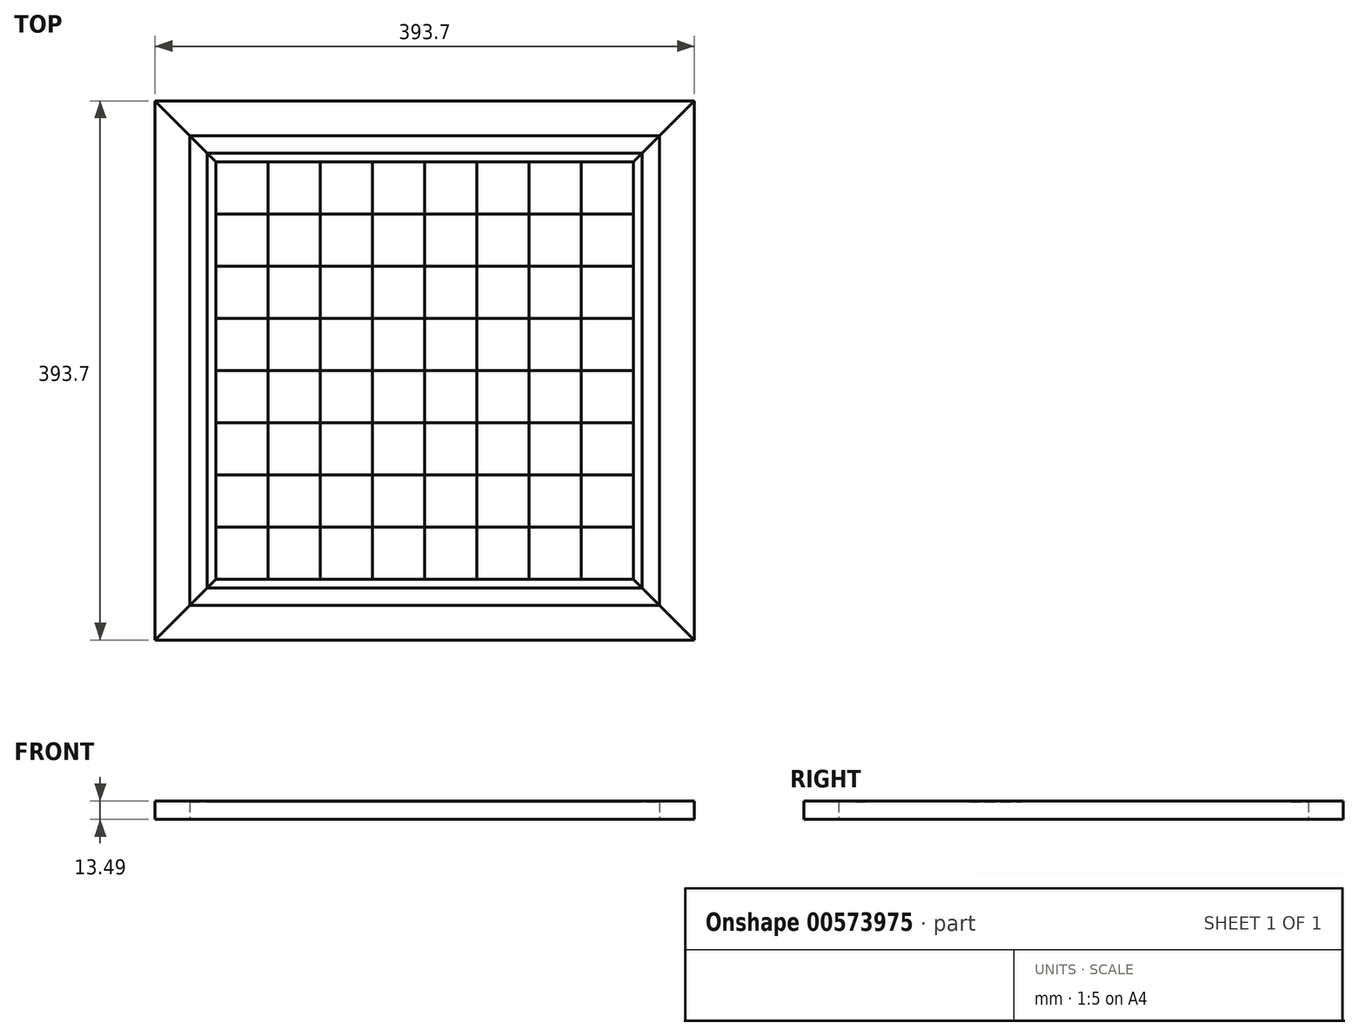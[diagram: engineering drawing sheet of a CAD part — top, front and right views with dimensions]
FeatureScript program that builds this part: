
annotation { "Feature Type Name" : "Feature", "Feature Type Description" : "" }
export const myFeature = defineFeature(function(context is Context, id is Id, definition is map)
    precondition{}
    {
        {
            var Q0;
            Q0=qCreatedBy(makeId("Top.planeOp"),FACE);
            var sketch = newSketch(context, id + "F0", { "sketchPlane" : qUnion([Q0])});
            skLineSegment(sketch, "E0.bottom", {"start": v(-171.45, 171.45) * mm, "end": v(171.45, 171.45) * mm});
            skLineSegment(sketch, "E0.top", {"start": v(-171.45, -171.45) * mm, "end": v(171.45, -171.45) * mm});
            skLineSegment(sketch, "E0.left", {"start": v(-171.45, 171.45) * mm, "end": v(-171.45, -171.45) * mm});
            skLineSegment(sketch, "E0.right", {"start": v(171.45, 171.45) * mm, "end": v(171.45, -171.45) * mm});
            skPoint(sketch, "E0.middle", {"position": v(0, 0) * mm});
            skSolve(sketch);
        }
        {
            var Q0;
            Q0 = qSketchRegion(id + "F0", true);
            extrude(context, id + "F1", {"entities" : qUnion([Q0]), "depth" : 12.7 * mm, "offsetDistance" : 25.4 * mm});
        }
        {
            var Q0;
            Q0=makeQuery(id+"F1.opExtrude","CAP_FACE",FACE,{"disambiguationData":[OSD([sQuery(id+"F0.wireOp",EDGE,"E0.bottom"),sQuery(id+"F0.wireOp",EDGE,"E0.top"),sQuery(id+"F0.wireOp",EDGE,"E0.left"),sQuery(id+"F0.wireOp",EDGE,"E0.right")])],"isStart":false});
            var sketch = newSketch(context, id + "F2", { "sketchPlane" : qUnion([Q0])});
            skLineSegment(sketch, "E1", {"start": v(152.4, 152.4) * mm, "end": v(152.4, -152.4) * mm});
            skLineSegment(sketch, "E2", {"start": v(171.45, -171.45) * mm, "end": v(152.4, -152.4) * mm});
            skLineSegment(sketch, "E3", {"start": v(171.45, 171.45) * mm, "end": v(152.4, 152.4) * mm});
            skLineSegment(sketch, "E4", {"start": v(152.4, 152.4) * mm, "end": v(-152.4, 152.4) * mm});
            skLineSegment(sketch, "E5", {"start": v(-152.4, 152.4) * mm, "end": v(-152.4, -152.4) * mm});
            skLineSegment(sketch, "E6", {"start": v(-152.4, -152.4) * mm, "end": v(152.4, -152.4) * mm});
            skLineSegment(sketch, "E7.trimOffspring", {"start": v(-152.4, -152.4) * mm, "end": v(-171.45, -171.45) * mm});
            skLineSegment(sketch, "E8.trimOffspring", {"start": v(-152.4, 152.4) * mm, "end": v(-171.45, 171.45) * mm});
            skLineSegment(sketch, "E9", {"start": v(158.75, 158.75) * mm, "end": v(158.75, -158.75) * mm});
            skLineSegment(sketch, "E10", {"start": v(158.75, 158.75) * mm, "end": v(-158.75, 158.75) * mm});
            skLineSegment(sketch, "E11", {"start": v(-158.75, 158.75) * mm, "end": v(-158.75, -158.75) * mm});
            skLineSegment(sketch, "E12", {"start": v(-158.75, -158.75) * mm, "end": v(158.75, -158.75) * mm});
            skLineSegment(sketch, "E13", {"start": v(152.4, 114.3) * mm, "end": v(-152.4, 114.3) * mm});
            skLineSegment(sketch, "E14", {"start": v(152.4, 76.2) * mm, "end": v(-152.4, 76.2) * mm});
            skLineSegment(sketch, "E15", {"start": v(152.4, 38.1) * mm, "end": v(-152.4, 38.1) * mm});
            skLineSegment(sketch, "E16", {"start": v(152.4, 0) * mm, "end": v(-152.4, 0) * mm});
            skLineSegment(sketch, "E17", {"start": v(152.4, -38.1) * mm, "end": v(-152.4, -38.1) * mm});
            skLineSegment(sketch, "E18", {"start": v(152.4, -76.2) * mm, "end": v(-152.4, -76.2) * mm});
            skLineSegment(sketch, "E19", {"start": v(-152.4, -114.3) * mm, "end": v(152.4, -114.3) * mm});
            skLineSegment(sketch, "E20", {"start": v(114.3, 152.4) * mm, "end": v(114.3, -152.4) * mm});
            skLineSegment(sketch, "E21", {"start": v(76.2, 152.4) * mm, "end": v(76.2, -152.4) * mm});
            skLineSegment(sketch, "E22", {"start": v(38.1, 152.4) * mm, "end": v(38.1, -152.4) * mm});
            skLineSegment(sketch, "E23", {"start": v(-114.3, 152.4) * mm, "end": v(-114.3, -152.4) * mm});
            skLineSegment(sketch, "E24", {"start": v(0, 152.4) * mm, "end": v(0, -152.4) * mm});
            skLineSegment(sketch, "E25", {"start": v(-38.1, 152.4) * mm, "end": v(-38.1, -152.4) * mm});
            skLineSegment(sketch, "E26", {"start": v(-76.2, -152.4) * mm, "end": v(-76.2, 152.4) * mm});
            skSolve(sketch);
        }
        {
            var Q0;
            {var subQ1=sQuery(id+"F2.wireOp",EDGE,"E1");var subQ3=sQuery(id+"F2.wireOp",EDGE,"E13");var subQ4=makeQuery(id+"F2.imprint","INTERSECT",VERTEX,{"derivedFrom":[subQ1,subQ3]});Q0=makeQuery(id+"F2.imprint","IMPRINT",FACE,{"disambiguationData":[TD([[makeQuery(id+"F2.imprint","IMPRINT",EDGE,{"disambiguationData":[TD([[subQ4,-1.0]])],"derivedFrom":subQ3}),-1.0]])]});}
            var Q1;
            {var subQ0=sQuery(id+"F2.wireOp",EDGE,"E14");var subQ1=sQuery(id+"F2.wireOp",EDGE,"E1");var subQ2=makeQuery(id+"F2.imprint","INTERSECT",VERTEX,{"derivedFrom":[subQ1,subQ0]});Q1=makeQuery(id+"F2.imprint","IMPRINT",FACE,{"disambiguationData":[TD([[makeQuery(id+"F2.imprint","IMPRINT",EDGE,{"disambiguationData":[TD([[subQ2,-1.0]])],"derivedFrom":subQ1}),-1.0]])]});}
            var Q2;
            {var subQ0=sQuery(id+"F2.wireOp",EDGE,"E16");var subQ1=sQuery(id+"F2.wireOp",EDGE,"E1");var subQ2=makeQuery(id+"F2.imprint","INTERSECT",VERTEX,{"derivedFrom":[subQ1,subQ0]});Q2=makeQuery(id+"F2.imprint","IMPRINT",FACE,{"disambiguationData":[TD([[makeQuery(id+"F2.imprint","IMPRINT",EDGE,{"disambiguationData":[TD([[subQ2,-1.0]])],"derivedFrom":subQ1}),-1.0]])]});}
            var Q3;
            {var subQ0=sQuery(id+"F2.wireOp",EDGE,"E18");var subQ1=sQuery(id+"F2.wireOp",EDGE,"E1");var subQ2=makeQuery(id+"F2.imprint","INTERSECT",VERTEX,{"derivedFrom":[subQ1,subQ0]});Q3=makeQuery(id+"F2.imprint","IMPRINT",FACE,{"disambiguationData":[TD([[makeQuery(id+"F2.imprint","IMPRINT",EDGE,{"disambiguationData":[TD([[subQ2,-1.0]])],"derivedFrom":subQ1}),-1.0]])]});}
            var Q4;
            {var subQ0=sQuery(id+"F2.wireOp",EDGE,"E20");var subQ1=sQuery(id+"F2.wireOp",EDGE,"E6");var subQ2=makeQuery(id+"F2.imprint","INTERSECT",VERTEX,{"derivedFrom":[subQ1,subQ0]});Q4=makeQuery(id+"F2.imprint","IMPRINT",FACE,{"disambiguationData":[TD([[makeQuery(id+"F2.imprint","IMPRINT",EDGE,{"disambiguationData":[TD([[subQ2,1.0]])],"derivedFrom":subQ1}),1.0]])]});}
            var Q5;
            {var subQ0=sQuery(id+"F2.wireOp",EDGE,"E20");var subQ1=sQuery(id+"F2.wireOp",EDGE,"E17");var subQ2=makeQuery(id+"F2.imprint","INTERSECT",VERTEX,{"derivedFrom":[subQ1,subQ0]});Q5=makeQuery(id+"F2.imprint","IMPRINT",FACE,{"disambiguationData":[TD([[makeQuery(id+"F2.imprint","IMPRINT",EDGE,{"disambiguationData":[TD([[subQ2,-1.0]])],"derivedFrom":subQ1}),1.0]])]});}
            var Q6;
            {var subQ0=sQuery(id+"F2.wireOp",EDGE,"E20");var subQ1=sQuery(id+"F2.wireOp",EDGE,"E15");var subQ2=makeQuery(id+"F2.imprint","INTERSECT",VERTEX,{"derivedFrom":[subQ1,subQ0]});Q6=makeQuery(id+"F2.imprint","IMPRINT",FACE,{"disambiguationData":[TD([[makeQuery(id+"F2.imprint","IMPRINT",EDGE,{"disambiguationData":[TD([[subQ2,-1.0]])],"derivedFrom":subQ1}),1.0]])]});}
            var Q7;
            {var subQ0=sQuery(id+"F2.wireOp",EDGE,"E20");var subQ1=sQuery(id+"F2.wireOp",EDGE,"E13");var subQ2=makeQuery(id+"F2.imprint","INTERSECT",VERTEX,{"derivedFrom":[subQ1,subQ0]});Q7=makeQuery(id+"F2.imprint","IMPRINT",FACE,{"disambiguationData":[TD([[makeQuery(id+"F2.imprint","IMPRINT",EDGE,{"disambiguationData":[TD([[subQ2,-1.0]])],"derivedFrom":subQ1}),1.0]])]});}
            var Q8;
            {var subQ0=sQuery(id+"F2.wireOp",EDGE,"E21");var subQ1=sQuery(id+"F2.wireOp",EDGE,"E4");var subQ2=makeQuery(id+"F2.imprint","INTERSECT",VERTEX,{"derivedFrom":[subQ1,subQ0]});Q8=makeQuery(id+"F2.imprint","IMPRINT",FACE,{"disambiguationData":[TD([[makeQuery(id+"F2.imprint","IMPRINT",EDGE,{"disambiguationData":[TD([[subQ2,-1.0]])],"derivedFrom":subQ1}),1.0]])]});}
            var Q9;
            {var subQ0=sQuery(id+"F2.wireOp",EDGE,"E21");var subQ1=sQuery(id+"F2.wireOp",EDGE,"E14");var subQ2=makeQuery(id+"F2.imprint","INTERSECT",VERTEX,{"derivedFrom":[subQ1,subQ0]});Q9=makeQuery(id+"F2.imprint","IMPRINT",FACE,{"disambiguationData":[TD([[makeQuery(id+"F2.imprint","IMPRINT",EDGE,{"disambiguationData":[TD([[subQ2,-1.0]])],"derivedFrom":subQ1}),1.0]])]});}
            var Q10;
            {var subQ0=sQuery(id+"F2.wireOp",EDGE,"E21");var subQ1=sQuery(id+"F2.wireOp",EDGE,"E16");var subQ2=makeQuery(id+"F2.imprint","INTERSECT",VERTEX,{"derivedFrom":[subQ1,subQ0]});Q10=makeQuery(id+"F2.imprint","IMPRINT",FACE,{"disambiguationData":[TD([[makeQuery(id+"F2.imprint","IMPRINT",EDGE,{"disambiguationData":[TD([[subQ2,-1.0]])],"derivedFrom":subQ1}),1.0]])]});}
            var Q11;
            {var subQ0=sQuery(id+"F2.wireOp",EDGE,"E21");var subQ1=sQuery(id+"F2.wireOp",EDGE,"E18");var subQ2=makeQuery(id+"F2.imprint","INTERSECT",VERTEX,{"derivedFrom":[subQ1,subQ0]});Q11=makeQuery(id+"F2.imprint","IMPRINT",FACE,{"disambiguationData":[TD([[makeQuery(id+"F2.imprint","IMPRINT",EDGE,{"disambiguationData":[TD([[subQ2,-1.0]])],"derivedFrom":subQ1}),1.0]])]});}
            var Q12;
            {var subQ0=sQuery(id+"F2.wireOp",EDGE,"E22");var subQ1=sQuery(id+"F2.wireOp",EDGE,"E13");var subQ2=makeQuery(id+"F2.imprint","INTERSECT",VERTEX,{"derivedFrom":[subQ1,subQ0]});Q12=makeQuery(id+"F2.imprint","IMPRINT",FACE,{"disambiguationData":[TD([[makeQuery(id+"F2.imprint","IMPRINT",EDGE,{"disambiguationData":[TD([[subQ2,-1.0]])],"derivedFrom":subQ1}),1.0]])]});}
            var Q13;
            {var subQ0=sQuery(id+"F2.wireOp",EDGE,"E22");var subQ1=sQuery(id+"F2.wireOp",EDGE,"E15");var subQ2=makeQuery(id+"F2.imprint","INTERSECT",VERTEX,{"derivedFrom":[subQ1,subQ0]});Q13=makeQuery(id+"F2.imprint","IMPRINT",FACE,{"disambiguationData":[TD([[makeQuery(id+"F2.imprint","IMPRINT",EDGE,{"disambiguationData":[TD([[subQ2,-1.0]])],"derivedFrom":subQ1}),1.0]])]});}
            var Q14;
            {var subQ0=sQuery(id+"F2.wireOp",EDGE,"E22");var subQ1=sQuery(id+"F2.wireOp",EDGE,"E17");var subQ2=makeQuery(id+"F2.imprint","INTERSECT",VERTEX,{"derivedFrom":[subQ1,subQ0]});Q14=makeQuery(id+"F2.imprint","IMPRINT",FACE,{"disambiguationData":[TD([[makeQuery(id+"F2.imprint","IMPRINT",EDGE,{"disambiguationData":[TD([[subQ2,-1.0]])],"derivedFrom":subQ1}),1.0]])]});}
            var Q15;
            {var subQ0=sQuery(id+"F2.wireOp",EDGE,"E22");var subQ1=sQuery(id+"F2.wireOp",EDGE,"E6");var subQ2=makeQuery(id+"F2.imprint","INTERSECT",VERTEX,{"derivedFrom":[subQ1,subQ0]});Q15=makeQuery(id+"F2.imprint","IMPRINT",FACE,{"disambiguationData":[TD([[makeQuery(id+"F2.imprint","IMPRINT",EDGE,{"disambiguationData":[TD([[subQ2,1.0]])],"derivedFrom":subQ1}),1.0]])]});}
            var Q16;
            {var subQ0=sQuery(id+"F2.wireOp",EDGE,"E24");var subQ1=sQuery(id+"F2.wireOp",EDGE,"E18");var subQ2=makeQuery(id+"F2.imprint","INTERSECT",VERTEX,{"derivedFrom":[subQ1,subQ0]});Q16=makeQuery(id+"F2.imprint","IMPRINT",FACE,{"disambiguationData":[TD([[makeQuery(id+"F2.imprint","IMPRINT",EDGE,{"disambiguationData":[TD([[subQ2,-1.0]])],"derivedFrom":subQ1}),1.0]])]});}
            var Q17;
            {var subQ0=sQuery(id+"F2.wireOp",EDGE,"E24");var subQ1=sQuery(id+"F2.wireOp",EDGE,"E16");var subQ2=makeQuery(id+"F2.imprint","INTERSECT",VERTEX,{"derivedFrom":[subQ1,subQ0]});Q17=makeQuery(id+"F2.imprint","IMPRINT",FACE,{"disambiguationData":[TD([[makeQuery(id+"F2.imprint","IMPRINT",EDGE,{"disambiguationData":[TD([[subQ2,-1.0]])],"derivedFrom":subQ1}),1.0]])]});}
            var Q18;
            {var subQ0=sQuery(id+"F2.wireOp",EDGE,"E24");var subQ1=sQuery(id+"F2.wireOp",EDGE,"E14");var subQ2=makeQuery(id+"F2.imprint","INTERSECT",VERTEX,{"derivedFrom":[subQ1,subQ0]});Q18=makeQuery(id+"F2.imprint","IMPRINT",FACE,{"disambiguationData":[TD([[makeQuery(id+"F2.imprint","IMPRINT",EDGE,{"disambiguationData":[TD([[subQ2,-1.0]])],"derivedFrom":subQ1}),1.0]])]});}
            var Q19;
            {var subQ0=sQuery(id+"F2.wireOp",EDGE,"E24");var subQ1=sQuery(id+"F2.wireOp",EDGE,"E4");var subQ2=makeQuery(id+"F2.imprint","INTERSECT",VERTEX,{"derivedFrom":[subQ1,subQ0]});Q19=makeQuery(id+"F2.imprint","IMPRINT",FACE,{"disambiguationData":[TD([[makeQuery(id+"F2.imprint","IMPRINT",EDGE,{"disambiguationData":[TD([[subQ2,-1.0]])],"derivedFrom":subQ1}),1.0]])]});}
            var Q20;
            {var subQ0=sQuery(id+"F2.wireOp",EDGE,"E25");var subQ1=sQuery(id+"F2.wireOp",EDGE,"E13");var subQ2=makeQuery(id+"F2.imprint","INTERSECT",VERTEX,{"derivedFrom":[subQ1,subQ0]});Q20=makeQuery(id+"F2.imprint","IMPRINT",FACE,{"disambiguationData":[TD([[makeQuery(id+"F2.imprint","IMPRINT",EDGE,{"disambiguationData":[TD([[subQ2,-1.0]])],"derivedFrom":subQ1}),1.0]])]});}
            var Q21;
            {var subQ0=sQuery(id+"F2.wireOp",EDGE,"E25");var subQ1=sQuery(id+"F2.wireOp",EDGE,"E15");var subQ2=makeQuery(id+"F2.imprint","INTERSECT",VERTEX,{"derivedFrom":[subQ1,subQ0]});Q21=makeQuery(id+"F2.imprint","IMPRINT",FACE,{"disambiguationData":[TD([[makeQuery(id+"F2.imprint","IMPRINT",EDGE,{"disambiguationData":[TD([[subQ2,-1.0]])],"derivedFrom":subQ1}),1.0]])]});}
            var Q22;
            {var subQ0=sQuery(id+"F2.wireOp",EDGE,"E25");var subQ1=sQuery(id+"F2.wireOp",EDGE,"E17");var subQ2=makeQuery(id+"F2.imprint","INTERSECT",VERTEX,{"derivedFrom":[subQ1,subQ0]});Q22=makeQuery(id+"F2.imprint","IMPRINT",FACE,{"disambiguationData":[TD([[makeQuery(id+"F2.imprint","IMPRINT",EDGE,{"disambiguationData":[TD([[subQ2,-1.0]])],"derivedFrom":subQ1}),1.0]])]});}
            var Q23;
            {var subQ0=sQuery(id+"F2.wireOp",EDGE,"E25");var subQ1=sQuery(id+"F2.wireOp",EDGE,"E6");var subQ2=makeQuery(id+"F2.imprint","INTERSECT",VERTEX,{"derivedFrom":[subQ1,subQ0]});Q23=makeQuery(id+"F2.imprint","IMPRINT",FACE,{"disambiguationData":[TD([[makeQuery(id+"F2.imprint","IMPRINT",EDGE,{"disambiguationData":[TD([[subQ2,1.0]])],"derivedFrom":subQ1}),1.0]])]});}
            var Q24;
            {var subQ0=sQuery(id+"F2.wireOp",EDGE,"E26");var subQ1=sQuery(id+"F2.wireOp",EDGE,"E18");var subQ2=makeQuery(id+"F2.imprint","INTERSECT",VERTEX,{"derivedFrom":[subQ1,subQ0]});Q24=makeQuery(id+"F2.imprint","IMPRINT",FACE,{"disambiguationData":[TD([[makeQuery(id+"F2.imprint","IMPRINT",EDGE,{"disambiguationData":[TD([[subQ2,-1.0]])],"derivedFrom":subQ1}),1.0]])]});}
            var Q25;
            {var subQ0=sQuery(id+"F2.wireOp",EDGE,"E26");var subQ1=sQuery(id+"F2.wireOp",EDGE,"E16");var subQ2=makeQuery(id+"F2.imprint","INTERSECT",VERTEX,{"derivedFrom":[subQ1,subQ0]});Q25=makeQuery(id+"F2.imprint","IMPRINT",FACE,{"disambiguationData":[TD([[makeQuery(id+"F2.imprint","IMPRINT",EDGE,{"disambiguationData":[TD([[subQ2,-1.0]])],"derivedFrom":subQ1}),1.0]])]});}
            var Q26;
            {var subQ0=sQuery(id+"F2.wireOp",EDGE,"E26");var subQ1=sQuery(id+"F2.wireOp",EDGE,"E14");var subQ2=makeQuery(id+"F2.imprint","INTERSECT",VERTEX,{"derivedFrom":[subQ1,subQ0]});Q26=makeQuery(id+"F2.imprint","IMPRINT",FACE,{"disambiguationData":[TD([[makeQuery(id+"F2.imprint","IMPRINT",EDGE,{"disambiguationData":[TD([[subQ2,-1.0]])],"derivedFrom":subQ1}),1.0]])]});}
            var Q27;
            {var subQ0=sQuery(id+"F2.wireOp",EDGE,"E23");var subQ1=sQuery(id+"F2.wireOp",EDGE,"E4");var subQ2=makeQuery(id+"F2.imprint","INTERSECT",VERTEX,{"derivedFrom":[subQ1,subQ0]});Q27=makeQuery(id+"F2.imprint","IMPRINT",FACE,{"disambiguationData":[TD([[makeQuery(id+"F2.imprint","IMPRINT",EDGE,{"disambiguationData":[TD([[subQ2,1.0]])],"derivedFrom":subQ1}),1.0]])]});}
            var Q28;
            {var subQ0=sQuery(id+"F2.wireOp",EDGE,"E13");var subQ1=sQuery(id+"F2.wireOp",EDGE,"E5");var subQ2=makeQuery(id+"F2.imprint","INTERSECT",VERTEX,{"derivedFrom":[subQ1,subQ0]});Q28=makeQuery(id+"F2.imprint","IMPRINT",FACE,{"disambiguationData":[TD([[makeQuery(id+"F2.imprint","IMPRINT",EDGE,{"disambiguationData":[TD([[subQ2,-1.0]])],"derivedFrom":subQ1}),1.0]])]});}
            var Q29;
            {var subQ0=sQuery(id+"F2.wireOp",EDGE,"E15");var subQ1=sQuery(id+"F2.wireOp",EDGE,"E5");var subQ2=makeQuery(id+"F2.imprint","INTERSECT",VERTEX,{"derivedFrom":[subQ1,subQ0]});Q29=makeQuery(id+"F2.imprint","IMPRINT",FACE,{"disambiguationData":[TD([[makeQuery(id+"F2.imprint","IMPRINT",EDGE,{"disambiguationData":[TD([[subQ2,-1.0]])],"derivedFrom":subQ1}),1.0]])]});}
            var Q30;
            {var subQ0=sQuery(id+"F2.wireOp",EDGE,"E17");var subQ1=sQuery(id+"F2.wireOp",EDGE,"E5");var subQ2=makeQuery(id+"F2.imprint","INTERSECT",VERTEX,{"derivedFrom":[subQ1,subQ0]});Q30=makeQuery(id+"F2.imprint","IMPRINT",FACE,{"disambiguationData":[TD([[makeQuery(id+"F2.imprint","IMPRINT",EDGE,{"disambiguationData":[TD([[subQ2,-1.0]])],"derivedFrom":subQ1}),1.0]])]});}
            var Q31;
            {var subQ1=sQuery(id+"F2.wireOp",EDGE,"E5");var subQ3=sQuery(id+"F2.wireOp",EDGE,"E19");var subQ4=makeQuery(id+"F2.imprint","INTERSECT",VERTEX,{"derivedFrom":[subQ1,subQ3]});Q31=makeQuery(id+"F2.imprint","IMPRINT",FACE,{"disambiguationData":[TD([[makeQuery(id+"F2.imprint","IMPRINT",EDGE,{"disambiguationData":[TD([[subQ4,-1.0]])],"derivedFrom":subQ3}),-1.0]])]});}
            extrude(context, id + "F3", {"entities" : qUnion([Q0, Q1, Q2, Q3, Q4, Q5, Q6, Q7, Q8, Q9, Q10, Q11, Q12, Q13, Q14, Q15, Q16, Q17, Q18, Q19, Q20, Q21, Q22, Q23, Q24, Q25, Q26, Q27, Q28, Q29, Q30, Q31]), "depth" : 0.8 * mm, "offsetDistance" : 25.4 * mm});
        }
        {
            var Q0;
            {var subQ0=sQuery(id+"F2.wireOp",EDGE,"E13");var subQ1=sQuery(id+"F2.wireOp",EDGE,"E1");var subQ2=makeQuery(id+"F2.imprint","INTERSECT",VERTEX,{"derivedFrom":[subQ1,subQ0]});Q0=makeQuery(id+"F2.imprint","IMPRINT",FACE,{"disambiguationData":[TD([[makeQuery(id+"F2.imprint","IMPRINT",EDGE,{"disambiguationData":[TD([[subQ2,-1.0]])],"derivedFrom":subQ1}),-1.0]])]});}
            var Q1;
            {var subQ0=sQuery(id+"F2.wireOp",EDGE,"E15");var subQ1=sQuery(id+"F2.wireOp",EDGE,"E1");var subQ2=makeQuery(id+"F2.imprint","INTERSECT",VERTEX,{"derivedFrom":[subQ1,subQ0]});Q1=makeQuery(id+"F2.imprint","IMPRINT",FACE,{"disambiguationData":[TD([[makeQuery(id+"F2.imprint","IMPRINT",EDGE,{"disambiguationData":[TD([[subQ2,-1.0]])],"derivedFrom":subQ1}),-1.0]])]});}
            var Q2;
            {var subQ0=sQuery(id+"F2.wireOp",EDGE,"E17");var subQ1=sQuery(id+"F2.wireOp",EDGE,"E1");var subQ2=makeQuery(id+"F2.imprint","INTERSECT",VERTEX,{"derivedFrom":[subQ1,subQ0]});Q2=makeQuery(id+"F2.imprint","IMPRINT",FACE,{"disambiguationData":[TD([[makeQuery(id+"F2.imprint","IMPRINT",EDGE,{"disambiguationData":[TD([[subQ2,-1.0]])],"derivedFrom":subQ1}),-1.0]])]});}
            var Q3;
            {var subQ1=sQuery(id+"F2.wireOp",EDGE,"E1");var subQ3=sQuery(id+"F2.wireOp",EDGE,"E19");var subQ4=makeQuery(id+"F2.imprint","INTERSECT",VERTEX,{"derivedFrom":[subQ1,subQ3]});Q3=makeQuery(id+"F2.imprint","IMPRINT",FACE,{"disambiguationData":[TD([[makeQuery(id+"F2.imprint","IMPRINT",EDGE,{"disambiguationData":[TD([[subQ4,1.0]])],"derivedFrom":subQ3}),-1.0]])]});}
            var Q4;
            {var subQ0=sQuery(id+"F2.wireOp",EDGE,"E20");var subQ1=sQuery(id+"F2.wireOp",EDGE,"E16");var subQ2=makeQuery(id+"F2.imprint","INTERSECT",VERTEX,{"derivedFrom":[subQ1,subQ0]});Q4=makeQuery(id+"F2.imprint","IMPRINT",FACE,{"disambiguationData":[TD([[makeQuery(id+"F2.imprint","IMPRINT",EDGE,{"disambiguationData":[TD([[subQ2,-1.0]])],"derivedFrom":subQ1}),1.0]])]});}
            var Q5;
            {var subQ0=sQuery(id+"F2.wireOp",EDGE,"E20");var subQ1=sQuery(id+"F2.wireOp",EDGE,"E14");var subQ2=makeQuery(id+"F2.imprint","INTERSECT",VERTEX,{"derivedFrom":[subQ1,subQ0]});Q5=makeQuery(id+"F2.imprint","IMPRINT",FACE,{"disambiguationData":[TD([[makeQuery(id+"F2.imprint","IMPRINT",EDGE,{"disambiguationData":[TD([[subQ2,-1.0]])],"derivedFrom":subQ1}),1.0]])]});}
            var Q6;
            {var subQ0=sQuery(id+"F2.wireOp",EDGE,"E20");var subQ1=sQuery(id+"F2.wireOp",EDGE,"E4");var subQ2=makeQuery(id+"F2.imprint","INTERSECT",VERTEX,{"derivedFrom":[subQ1,subQ0]});Q6=makeQuery(id+"F2.imprint","IMPRINT",FACE,{"disambiguationData":[TD([[makeQuery(id+"F2.imprint","IMPRINT",EDGE,{"disambiguationData":[TD([[subQ2,-1.0]])],"derivedFrom":subQ1}),1.0]])]});}
            var Q7;
            {var subQ0=sQuery(id+"F2.wireOp",EDGE,"E21");var subQ1=sQuery(id+"F2.wireOp",EDGE,"E13");var subQ2=makeQuery(id+"F2.imprint","INTERSECT",VERTEX,{"derivedFrom":[subQ1,subQ0]});Q7=makeQuery(id+"F2.imprint","IMPRINT",FACE,{"disambiguationData":[TD([[makeQuery(id+"F2.imprint","IMPRINT",EDGE,{"disambiguationData":[TD([[subQ2,-1.0]])],"derivedFrom":subQ1}),1.0]])]});}
            var Q8;
            {var subQ0=sQuery(id+"F2.wireOp",EDGE,"E21");var subQ1=sQuery(id+"F2.wireOp",EDGE,"E15");var subQ2=makeQuery(id+"F2.imprint","INTERSECT",VERTEX,{"derivedFrom":[subQ1,subQ0]});Q8=makeQuery(id+"F2.imprint","IMPRINT",FACE,{"disambiguationData":[TD([[makeQuery(id+"F2.imprint","IMPRINT",EDGE,{"disambiguationData":[TD([[subQ2,-1.0]])],"derivedFrom":subQ1}),1.0]])]});}
            var Q9;
            {var subQ0=sQuery(id+"F2.wireOp",EDGE,"E21");var subQ1=sQuery(id+"F2.wireOp",EDGE,"E17");var subQ2=makeQuery(id+"F2.imprint","INTERSECT",VERTEX,{"derivedFrom":[subQ1,subQ0]});Q9=makeQuery(id+"F2.imprint","IMPRINT",FACE,{"disambiguationData":[TD([[makeQuery(id+"F2.imprint","IMPRINT",EDGE,{"disambiguationData":[TD([[subQ2,-1.0]])],"derivedFrom":subQ1}),1.0]])]});}
            var Q10;
            {var subQ0=sQuery(id+"F2.wireOp",EDGE,"E21");var subQ1=sQuery(id+"F2.wireOp",EDGE,"E6");var subQ2=makeQuery(id+"F2.imprint","INTERSECT",VERTEX,{"derivedFrom":[subQ1,subQ0]});Q10=makeQuery(id+"F2.imprint","IMPRINT",FACE,{"disambiguationData":[TD([[makeQuery(id+"F2.imprint","IMPRINT",EDGE,{"disambiguationData":[TD([[subQ2,1.0]])],"derivedFrom":subQ1}),1.0]])]});}
            var Q11;
            {var subQ0=sQuery(id+"F2.wireOp",EDGE,"E20");var subQ1=sQuery(id+"F2.wireOp",EDGE,"E18");var subQ2=makeQuery(id+"F2.imprint","INTERSECT",VERTEX,{"derivedFrom":[subQ1,subQ0]});Q11=makeQuery(id+"F2.imprint","IMPRINT",FACE,{"disambiguationData":[TD([[makeQuery(id+"F2.imprint","IMPRINT",EDGE,{"disambiguationData":[TD([[subQ2,-1.0]])],"derivedFrom":subQ1}),1.0]])]});}
            var Q12;
            {var subQ0=sQuery(id+"F2.wireOp",EDGE,"E22");var subQ1=sQuery(id+"F2.wireOp",EDGE,"E18");var subQ2=makeQuery(id+"F2.imprint","INTERSECT",VERTEX,{"derivedFrom":[subQ1,subQ0]});Q12=makeQuery(id+"F2.imprint","IMPRINT",FACE,{"disambiguationData":[TD([[makeQuery(id+"F2.imprint","IMPRINT",EDGE,{"disambiguationData":[TD([[subQ2,-1.0]])],"derivedFrom":subQ1}),1.0]])]});}
            var Q13;
            {var subQ0=sQuery(id+"F2.wireOp",EDGE,"E22");var subQ1=sQuery(id+"F2.wireOp",EDGE,"E16");var subQ2=makeQuery(id+"F2.imprint","INTERSECT",VERTEX,{"derivedFrom":[subQ1,subQ0]});Q13=makeQuery(id+"F2.imprint","IMPRINT",FACE,{"disambiguationData":[TD([[makeQuery(id+"F2.imprint","IMPRINT",EDGE,{"disambiguationData":[TD([[subQ2,-1.0]])],"derivedFrom":subQ1}),1.0]])]});}
            var Q14;
            {var subQ0=sQuery(id+"F2.wireOp",EDGE,"E22");var subQ1=sQuery(id+"F2.wireOp",EDGE,"E14");var subQ2=makeQuery(id+"F2.imprint","INTERSECT",VERTEX,{"derivedFrom":[subQ1,subQ0]});Q14=makeQuery(id+"F2.imprint","IMPRINT",FACE,{"disambiguationData":[TD([[makeQuery(id+"F2.imprint","IMPRINT",EDGE,{"disambiguationData":[TD([[subQ2,-1.0]])],"derivedFrom":subQ1}),1.0]])]});}
            var Q15;
            {var subQ0=sQuery(id+"F2.wireOp",EDGE,"E22");var subQ1=sQuery(id+"F2.wireOp",EDGE,"E4");var subQ2=makeQuery(id+"F2.imprint","INTERSECT",VERTEX,{"derivedFrom":[subQ1,subQ0]});Q15=makeQuery(id+"F2.imprint","IMPRINT",FACE,{"disambiguationData":[TD([[makeQuery(id+"F2.imprint","IMPRINT",EDGE,{"disambiguationData":[TD([[subQ2,-1.0]])],"derivedFrom":subQ1}),1.0]])]});}
            var Q16;
            {var subQ0=sQuery(id+"F2.wireOp",EDGE,"E24");var subQ1=sQuery(id+"F2.wireOp",EDGE,"E13");var subQ2=makeQuery(id+"F2.imprint","INTERSECT",VERTEX,{"derivedFrom":[subQ1,subQ0]});Q16=makeQuery(id+"F2.imprint","IMPRINT",FACE,{"disambiguationData":[TD([[makeQuery(id+"F2.imprint","IMPRINT",EDGE,{"disambiguationData":[TD([[subQ2,-1.0]])],"derivedFrom":subQ1}),1.0]])]});}
            var Q17;
            {var subQ0=sQuery(id+"F2.wireOp",EDGE,"E24");var subQ1=sQuery(id+"F2.wireOp",EDGE,"E15");var subQ2=makeQuery(id+"F2.imprint","INTERSECT",VERTEX,{"derivedFrom":[subQ1,subQ0]});Q17=makeQuery(id+"F2.imprint","IMPRINT",FACE,{"disambiguationData":[TD([[makeQuery(id+"F2.imprint","IMPRINT",EDGE,{"disambiguationData":[TD([[subQ2,-1.0]])],"derivedFrom":subQ1}),1.0]])]});}
            var Q18;
            {var subQ0=sQuery(id+"F2.wireOp",EDGE,"E24");var subQ1=sQuery(id+"F2.wireOp",EDGE,"E17");var subQ2=makeQuery(id+"F2.imprint","INTERSECT",VERTEX,{"derivedFrom":[subQ1,subQ0]});Q18=makeQuery(id+"F2.imprint","IMPRINT",FACE,{"disambiguationData":[TD([[makeQuery(id+"F2.imprint","IMPRINT",EDGE,{"disambiguationData":[TD([[subQ2,-1.0]])],"derivedFrom":subQ1}),1.0]])]});}
            var Q19;
            {var subQ0=sQuery(id+"F2.wireOp",EDGE,"E24");var subQ1=sQuery(id+"F2.wireOp",EDGE,"E6");var subQ2=makeQuery(id+"F2.imprint","INTERSECT",VERTEX,{"derivedFrom":[subQ1,subQ0]});Q19=makeQuery(id+"F2.imprint","IMPRINT",FACE,{"disambiguationData":[TD([[makeQuery(id+"F2.imprint","IMPRINT",EDGE,{"disambiguationData":[TD([[subQ2,1.0]])],"derivedFrom":subQ1}),1.0]])]});}
            var Q20;
            {var subQ0=sQuery(id+"F2.wireOp",EDGE,"E25");var subQ1=sQuery(id+"F2.wireOp",EDGE,"E18");var subQ2=makeQuery(id+"F2.imprint","INTERSECT",VERTEX,{"derivedFrom":[subQ1,subQ0]});Q20=makeQuery(id+"F2.imprint","IMPRINT",FACE,{"disambiguationData":[TD([[makeQuery(id+"F2.imprint","IMPRINT",EDGE,{"disambiguationData":[TD([[subQ2,-1.0]])],"derivedFrom":subQ1}),1.0]])]});}
            var Q21;
            {var subQ0=sQuery(id+"F2.wireOp",EDGE,"E25");var subQ1=sQuery(id+"F2.wireOp",EDGE,"E16");var subQ2=makeQuery(id+"F2.imprint","INTERSECT",VERTEX,{"derivedFrom":[subQ1,subQ0]});Q21=makeQuery(id+"F2.imprint","IMPRINT",FACE,{"disambiguationData":[TD([[makeQuery(id+"F2.imprint","IMPRINT",EDGE,{"disambiguationData":[TD([[subQ2,-1.0]])],"derivedFrom":subQ1}),1.0]])]});}
            var Q22;
            {var subQ0=sQuery(id+"F2.wireOp",EDGE,"E25");var subQ1=sQuery(id+"F2.wireOp",EDGE,"E14");var subQ2=makeQuery(id+"F2.imprint","INTERSECT",VERTEX,{"derivedFrom":[subQ1,subQ0]});Q22=makeQuery(id+"F2.imprint","IMPRINT",FACE,{"disambiguationData":[TD([[makeQuery(id+"F2.imprint","IMPRINT",EDGE,{"disambiguationData":[TD([[subQ2,-1.0]])],"derivedFrom":subQ1}),1.0]])]});}
            var Q23;
            {var subQ0=sQuery(id+"F2.wireOp",EDGE,"E25");var subQ1=sQuery(id+"F2.wireOp",EDGE,"E4");var subQ2=makeQuery(id+"F2.imprint","INTERSECT",VERTEX,{"derivedFrom":[subQ1,subQ0]});Q23=makeQuery(id+"F2.imprint","IMPRINT",FACE,{"disambiguationData":[TD([[makeQuery(id+"F2.imprint","IMPRINT",EDGE,{"disambiguationData":[TD([[subQ2,-1.0]])],"derivedFrom":subQ1}),1.0]])]});}
            var Q24;
            {var subQ0=sQuery(id+"F2.wireOp",EDGE,"E26");var subQ1=sQuery(id+"F2.wireOp",EDGE,"E13");var subQ2=makeQuery(id+"F2.imprint","INTERSECT",VERTEX,{"derivedFrom":[subQ1,subQ0]});Q24=makeQuery(id+"F2.imprint","IMPRINT",FACE,{"disambiguationData":[TD([[makeQuery(id+"F2.imprint","IMPRINT",EDGE,{"disambiguationData":[TD([[subQ2,-1.0]])],"derivedFrom":subQ1}),1.0]])]});}
            var Q25;
            {var subQ0=sQuery(id+"F2.wireOp",EDGE,"E26");var subQ1=sQuery(id+"F2.wireOp",EDGE,"E15");var subQ2=makeQuery(id+"F2.imprint","INTERSECT",VERTEX,{"derivedFrom":[subQ1,subQ0]});Q25=makeQuery(id+"F2.imprint","IMPRINT",FACE,{"disambiguationData":[TD([[makeQuery(id+"F2.imprint","IMPRINT",EDGE,{"disambiguationData":[TD([[subQ2,-1.0]])],"derivedFrom":subQ1}),1.0]])]});}
            var Q26;
            {var subQ0=sQuery(id+"F2.wireOp",EDGE,"E26");var subQ1=sQuery(id+"F2.wireOp",EDGE,"E17");var subQ2=makeQuery(id+"F2.imprint","INTERSECT",VERTEX,{"derivedFrom":[subQ1,subQ0]});Q26=makeQuery(id+"F2.imprint","IMPRINT",FACE,{"disambiguationData":[TD([[makeQuery(id+"F2.imprint","IMPRINT",EDGE,{"disambiguationData":[TD([[subQ2,-1.0]])],"derivedFrom":subQ1}),1.0]])]});}
            var Q27;
            {var subQ0=sQuery(id+"F2.wireOp",EDGE,"E23");var subQ1=sQuery(id+"F2.wireOp",EDGE,"E6");var subQ2=makeQuery(id+"F2.imprint","INTERSECT",VERTEX,{"derivedFrom":[subQ1,subQ0]});Q27=makeQuery(id+"F2.imprint","IMPRINT",FACE,{"disambiguationData":[TD([[makeQuery(id+"F2.imprint","IMPRINT",EDGE,{"disambiguationData":[TD([[subQ2,-1.0]])],"derivedFrom":subQ1}),1.0]])]});}
            var Q28;
            {var subQ0=sQuery(id+"F2.wireOp",EDGE,"E18");var subQ1=sQuery(id+"F2.wireOp",EDGE,"E5");var subQ2=makeQuery(id+"F2.imprint","INTERSECT",VERTEX,{"derivedFrom":[subQ1,subQ0]});Q28=makeQuery(id+"F2.imprint","IMPRINT",FACE,{"disambiguationData":[TD([[makeQuery(id+"F2.imprint","IMPRINT",EDGE,{"disambiguationData":[TD([[subQ2,-1.0]])],"derivedFrom":subQ1}),1.0]])]});}
            var Q29;
            {var subQ0=sQuery(id+"F2.wireOp",EDGE,"E16");var subQ1=sQuery(id+"F2.wireOp",EDGE,"E5");var subQ2=makeQuery(id+"F2.imprint","INTERSECT",VERTEX,{"derivedFrom":[subQ1,subQ0]});Q29=makeQuery(id+"F2.imprint","IMPRINT",FACE,{"disambiguationData":[TD([[makeQuery(id+"F2.imprint","IMPRINT",EDGE,{"disambiguationData":[TD([[subQ2,-1.0]])],"derivedFrom":subQ1}),1.0]])]});}
            var Q30;
            {var subQ0=sQuery(id+"F2.wireOp",EDGE,"E14");var subQ1=sQuery(id+"F2.wireOp",EDGE,"E5");var subQ2=makeQuery(id+"F2.imprint","INTERSECT",VERTEX,{"derivedFrom":[subQ1,subQ0]});Q30=makeQuery(id+"F2.imprint","IMPRINT",FACE,{"disambiguationData":[TD([[makeQuery(id+"F2.imprint","IMPRINT",EDGE,{"disambiguationData":[TD([[subQ2,-1.0]])],"derivedFrom":subQ1}),1.0]])]});}
            var Q31;
            {var subQ0=sQuery(id+"F2.wireOp",EDGE,"E5");var subQ5=sQuery(id+"F2.wireOp",EDGE,"E13");var subQ7=makeQuery(id+"F2.imprint","INTERSECT",VERTEX,{"derivedFrom":[subQ0,subQ5]});Q31=makeQuery(id+"F2.imprint","IMPRINT",FACE,{"disambiguationData":[TD([[makeQuery(id+"F2.imprint","IMPRINT",EDGE,{"disambiguationData":[TD([[subQ7,1.0]])],"derivedFrom":subQ5}),-1.0]])]});}
            extrude(context, id + "F4", {"entities" : qUnion([Q0, Q1, Q2, Q3, Q4, Q5, Q6, Q7, Q8, Q9, Q10, Q11, Q12, Q13, Q14, Q15, Q16, Q17, Q18, Q19, Q20, Q21, Q22, Q23, Q24, Q25, Q26, Q27, Q28, Q29, Q30, Q31]), "depth" : 0.8 * mm, "offsetDistance" : 25.4 * mm});
        }
        {
            var Q0;
            {var subQ3=sQuery(id+"F2.wireOp",EDGE,"E9");Q0=makeQuery(id+"F2.imprint","IMPRINT",FACE,{"disambiguationData":[TD([[makeQuery(id+"F2.imprint","IMPRINT",EDGE,{"derivedFrom":subQ3}),-1.0]])]});}
            var Q1;
            {var subQ3=sQuery(id+"F2.wireOp",EDGE,"E11");Q1=makeQuery(id+"F2.imprint","IMPRINT",FACE,{"disambiguationData":[TD([[makeQuery(id+"F2.imprint","IMPRINT",EDGE,{"derivedFrom":subQ3}),1.0]])]});}
            extrude(context, id + "F5", {"entities" : qUnion([Q0, Q1]), "depth" : 0.8 * mm, "offsetDistance" : 25.4 * mm});
        }
        {
            var Q0;
            {var subQ2=sQuery(id+"F2.wireOp",EDGE,"E12");Q0=makeQuery(id+"F2.imprint","IMPRINT",FACE,{"disambiguationData":[TD([[makeQuery(id+"F2.imprint","IMPRINT",EDGE,{"derivedFrom":subQ2}),-1.0]])]});}
            var Q1;
            {var subQ2=sQuery(id+"F2.wireOp",EDGE,"E10");Q1=makeQuery(id+"F2.imprint","IMPRINT",FACE,{"disambiguationData":[TD([[makeQuery(id+"F2.imprint","IMPRINT",EDGE,{"derivedFrom":subQ2}),-1.0]])]});}
            extrude(context, id + "F6", {"entities" : qUnion([Q0, Q1]), "depth" : 0.8 * mm, "offsetDistance" : 25.4 * mm});
        }
        {
            var Q0;
            Q0=makeQuery(id+"F1.opExtrude","CAP_FACE",FACE,{"disambiguationData":[OSD([sQuery(id+"F0.wireOp",EDGE,"E0.bottom"),sQuery(id+"F0.wireOp",EDGE,"E0.top"),sQuery(id+"F0.wireOp",EDGE,"E0.left"),sQuery(id+"F0.wireOp",EDGE,"E0.right")])],"isStart":true});
            var sketch = newSketch(context, id + "F7", { "sketchPlane" : qUnion([Q0])});
            skLineSegment(sketch, "E27.0", {"start": v(171.45, -171.45) * mm, "end": v(171.45, 171.45) * mm});
            skLineSegment(sketch, "E28.0", {"start": v(-171.45, -171.45) * mm, "end": v(171.45, -171.45) * mm});
            skLineSegment(sketch, "E29.0", {"start": v(-171.45, -171.45) * mm, "end": v(-171.45, 171.45) * mm});
            skLineSegment(sketch, "E30.0", {"start": v(-171.45, 171.45) * mm, "end": v(171.45, 171.45) * mm});
            skLineSegment(sketch, "E31", {"start": v(196.85, 196.85) * mm, "end": v(196.85, -196.85) * mm});
            skLineSegment(sketch, "E32", {"start": v(171.45, 171.45) * mm, "end": v(196.85, 196.85) * mm});
            skLineSegment(sketch, "E33", {"start": v(196.85, 196.85) * mm, "end": v(-196.85, 196.85) * mm});
            skLineSegment(sketch, "E34", {"start": v(-196.85, 196.85) * mm, "end": v(-171.45, 171.45) * mm});
            skLineSegment(sketch, "E35", {"start": v(171.45, -171.45) * mm, "end": v(196.85, -196.85) * mm});
            skLineSegment(sketch, "E36", {"start": v(-196.85, 196.85) * mm, "end": v(-196.85, -196.85) * mm});
            skLineSegment(sketch, "E37", {"start": v(196.85, -196.85) * mm, "end": v(-196.85, -196.85) * mm});
            skLineSegment(sketch, "E38", {"start": v(-196.85, -196.85) * mm, "end": v(-171.45, -171.45) * mm});
            skSolve(sketch);
        }
        {
            var Q0;
            Q0=makeQuery(id+"F7.imprint","IMPRINT",FACE,{"disambiguationData":[TD([[makeQuery(id+"F7.imprint","IMPRINT",EDGE,{"derivedFrom":sQuery(id+"F7.wireOp",EDGE,"E29.0")}),1.0]])]});
            var Q1;
            Q1=makeQuery(id+"F7.imprint","IMPRINT",FACE,{"disambiguationData":[TD([[makeQuery(id+"F7.imprint","IMPRINT",EDGE,{"derivedFrom":sQuery(id+"F7.wireOp",EDGE,"E27.0")}),-1.0]])]});
            extrude(context, id + "F8", {"entities" : qUnion([Q0, Q1]), "oppositeDirection" : true, "depth" : 13.5 * mm, "offsetDistance" : 25.4 * mm});
        }
        {
            var Q0;
            Q0=makeQuery(id+"F7.imprint","IMPRINT",FACE,{"disambiguationData":[TD([[makeQuery(id+"F7.imprint","IMPRINT",EDGE,{"derivedFrom":sQuery(id+"F7.wireOp",EDGE,"E28.0")}),-1.0]])]});
            var Q1;
            Q1=makeQuery(id+"F7.imprint","IMPRINT",FACE,{"disambiguationData":[TD([[makeQuery(id+"F7.imprint","IMPRINT",EDGE,{"derivedFrom":sQuery(id+"F7.wireOp",EDGE,"E30.0")}),1.0]])]});
            extrude(context, id + "F9", {"entities" : qUnion([Q0, Q1]), "oppositeDirection" : true, "depth" : 13.5 * mm, "offsetDistance" : 25.4 * mm});
        }
        {
            var Q0;
            Q0=makeQuery(id+"F8.opExtrude","CAP_FACE",FACE,{"disambiguationData":[OSD([sQuery(id+"F7.wireOp",EDGE,"E29.0"),sQuery(id+"F7.wireOp",EDGE,"E34"),sQuery(id+"F7.wireOp",EDGE,"E36"),sQuery(id+"F7.wireOp",EDGE,"E38")])],"isStart":false});
            var sketch = newSketch(context, id + "F10", { "sketchPlane" : qUnion([Q0])});
            skPoint(sketch, "E39", {"position": v(-192.33, 192.33) * mm});
            skSolve(sketch);
        }
        {
            var Q0;
            {var subQ2=sQuery(id+"F2.wireOp",EDGE,"E11");Q0=makeQuery(id+"F2.imprint","IMPRINT",FACE,{"disambiguationData":[TD([[makeQuery(id+"F2.imprint","IMPRINT",EDGE,{"derivedFrom":subQ2}),-1.0]])]});}
            var Q1;
            {var subQ2=sQuery(id+"F2.wireOp",EDGE,"E9");Q1=makeQuery(id+"F2.imprint","IMPRINT",FACE,{"disambiguationData":[TD([[makeQuery(id+"F2.imprint","IMPRINT",EDGE,{"derivedFrom":subQ2}),1.0]])]});}
            extrude(context, id + "F11", {"entities" : qUnion([Q0, Q1]), "depth" : 0.8 * mm, "offsetDistance" : 25.4 * mm});
        }
        {
            var Q0;
            {var subQ3=sQuery(id+"F2.wireOp",EDGE,"E12");Q0=makeQuery(id+"F2.imprint","IMPRINT",FACE,{"disambiguationData":[TD([[makeQuery(id+"F2.imprint","IMPRINT",EDGE,{"derivedFrom":subQ3}),1.0]])]});}
            var Q1;
            {var subQ5=sQuery(id+"F2.wireOp",EDGE,"E10");Q1=makeQuery(id+"F2.imprint","IMPRINT",FACE,{"disambiguationData":[TD([[makeQuery(id+"F2.imprint","IMPRINT",EDGE,{"derivedFrom":subQ5}),1.0]])]});}
            extrude(context, id + "F12", {"entities" : qUnion([Q0, Q1]), "depth" : 0.8 * mm, "offsetDistance" : 25.4 * mm});
        }
    });
